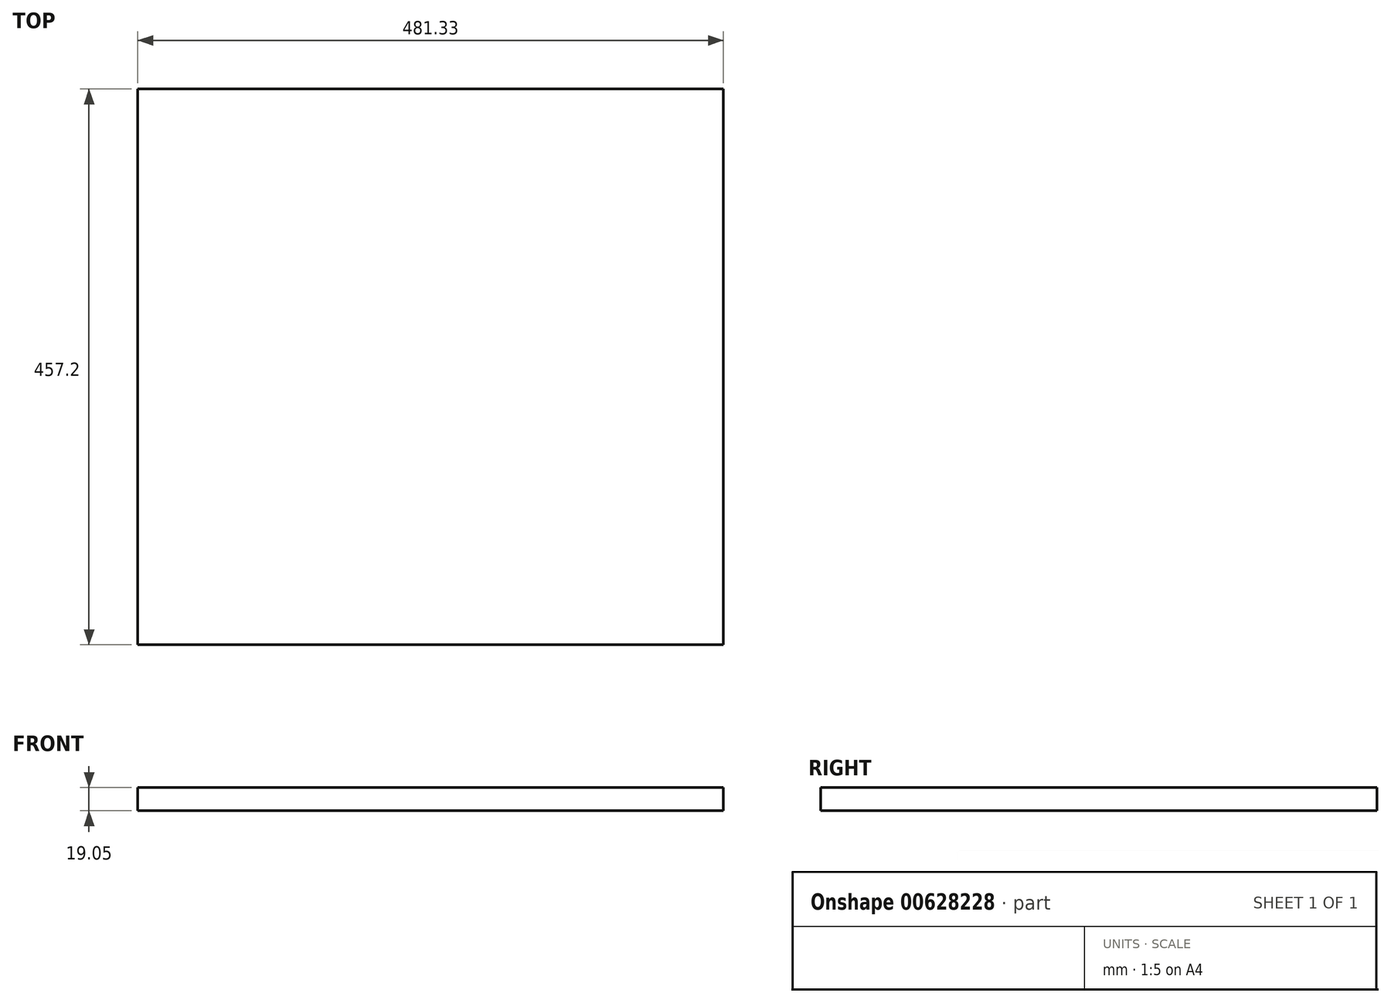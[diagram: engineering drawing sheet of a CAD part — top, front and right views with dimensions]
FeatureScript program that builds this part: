
annotation { "Feature Type Name" : "Feature", "Feature Type Description" : "" }
export const myFeature = defineFeature(function(context is Context, id is Id, definition is map)
    precondition{}
    {
        {
            var Q0;
            Q0=qCreatedBy(makeId("Top.planeOp"),FACE);
            var sketch = newSketch(context, id + "F0", { "sketchPlane" : qUnion([Q0])});
            skLineSegment(sketch, "E0.bottom", {"start": v(0, 0) * mm, "end": v(481.33, 0) * mm});
            skLineSegment(sketch, "E0.top", {"start": v(0, 457.2) * mm, "end": v(481.33, 457.2) * mm});
            skLineSegment(sketch, "E0.left", {"start": v(0, 0) * mm, "end": v(0, 457.2) * mm});
            skLineSegment(sketch, "E0.right", {"start": v(481.33, 0) * mm, "end": v(481.33, 457.2) * mm});
            skSolve(sketch);
        }
        {
            var Q0;
            Q0=makeQuery(id+"F0.imprint","IMPRINT",FACE,{"disambiguationData":[TD([[makeQuery(id+"F0.imprint","IMPRINT",EDGE,{"derivedFrom":sQuery(id+"F0.wireOp",EDGE,"E0.bottom")}),1.0]])]});
            extrude(context, id + "F1", {"entities" : qUnion([Q0]), "depth" : 19.05 * mm, "offsetDistance" : 25.4 * mm});
        }
    });
